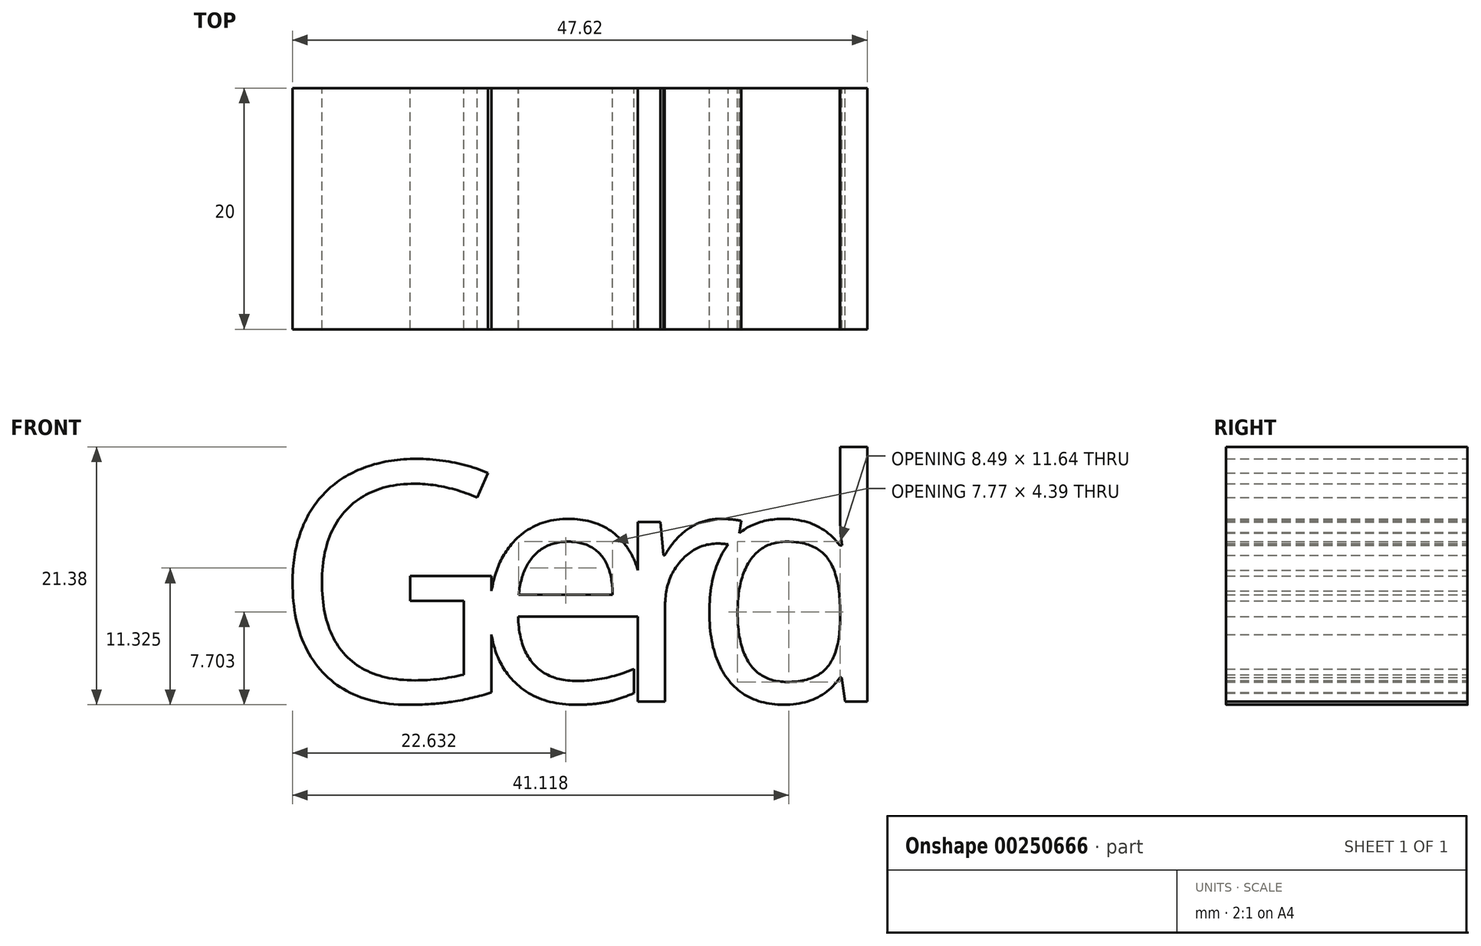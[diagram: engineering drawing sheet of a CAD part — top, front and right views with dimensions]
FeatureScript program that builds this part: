
annotation { "Feature Type Name" : "Feature", "Feature Type Description" : "" }
export const myFeature = defineFeature(function(context is Context, id is Id, definition is map)
    precondition{}
    {
        {
            var Q0;
            Q0=qCreatedBy(makeId("Front.planeOp"),FACE);
            var sketch = newSketch(context, id + "F0", { "sketchPlane" : qUnion([Q0])});
            skText(sketch, "E0", { "text": "G", "fontName": "OpenSans-Regular.ttf"});
            skText(sketch, "E1", { "text": "e", "fontName": "OpenSans-Regular.ttf"});
            skText(sketch, "E2", { "text": "r", "fontName": "OpenSans-Regular.ttf"});
            skText(sketch, "E3", { "text": "d", "fontName": "OpenSans-Regular.ttf"});
            const initialGuessF0  = {"E0": [-0.03863, 0, 1, 0, 0.02], "E1": [-0.02213, 0, 1, 0, 0.02], "E2": [-0.0107, 0, 1, 0, 0.02], "E3": [-0.00395, 0, 1, 0, 0.02]};
            skSetInitialGuess(sketch, initialGuessF0);
            skSolve(sketch);
        }
        {
            var Q0;
            Q0 = qSketchRegion(id + "F0", true);
            extrude(context, id + "F1", {"entities" : qUnion([Q0]), "depth" : 20 * mm});
        }
    });
